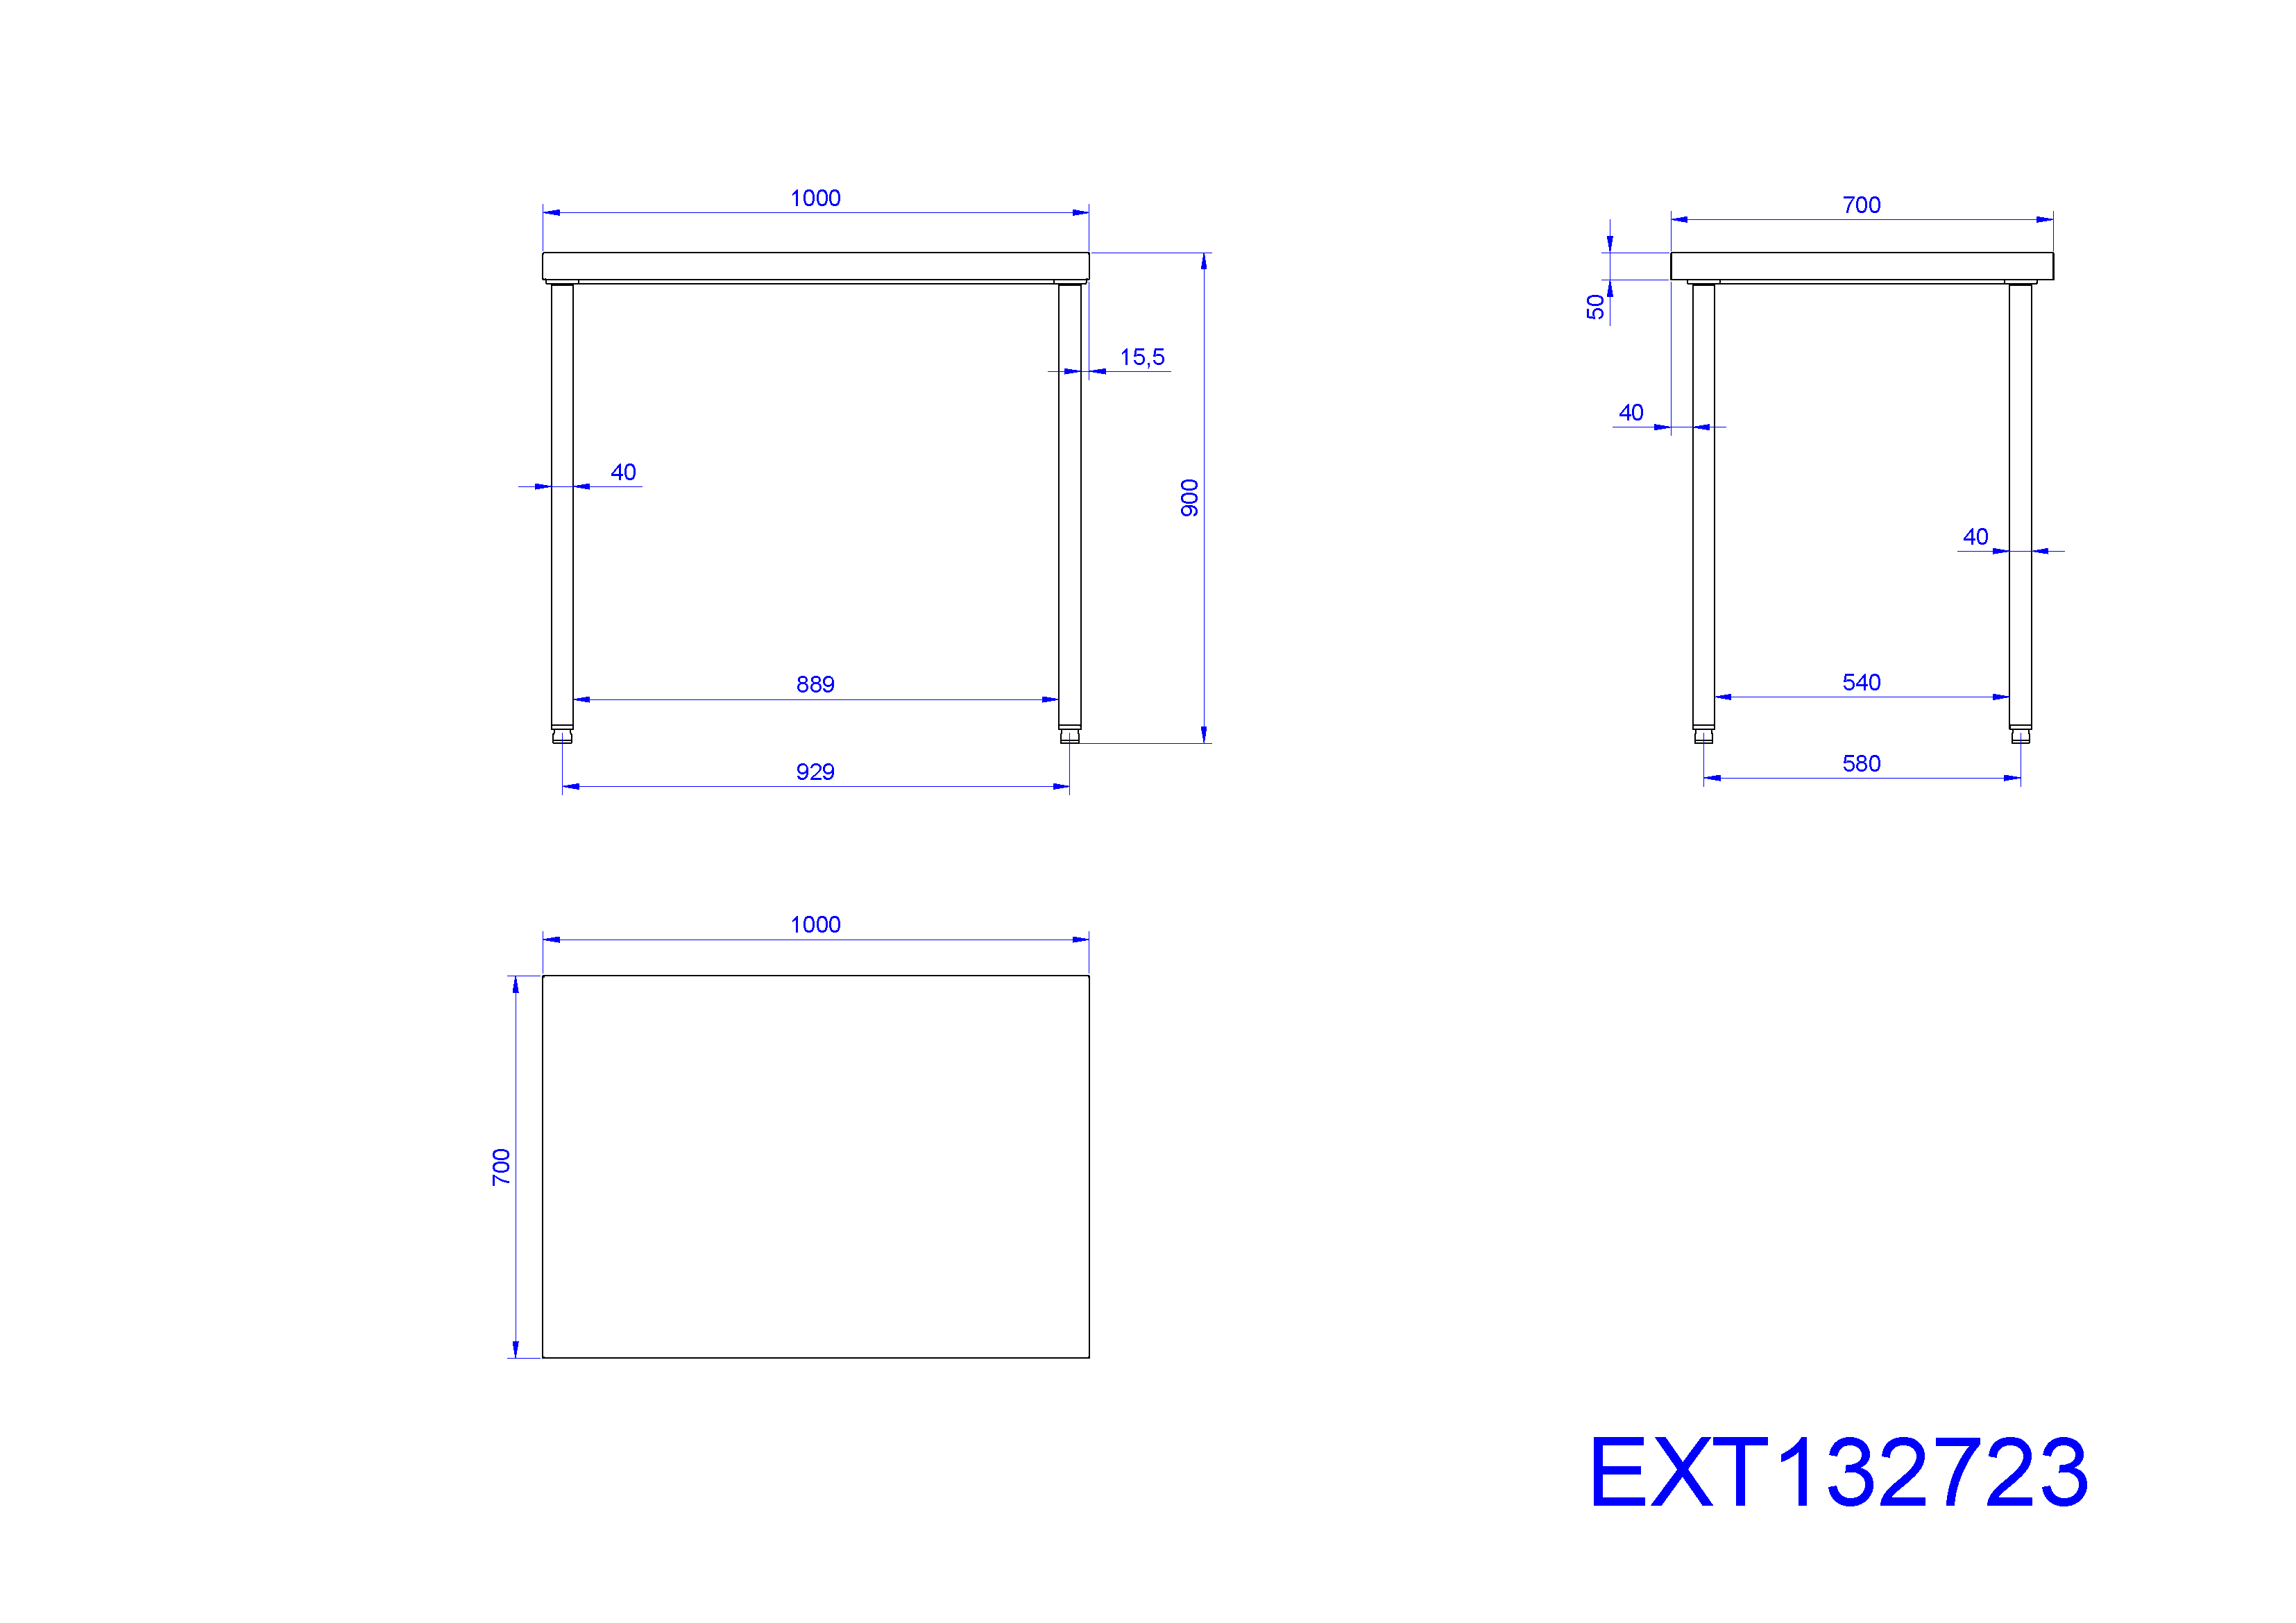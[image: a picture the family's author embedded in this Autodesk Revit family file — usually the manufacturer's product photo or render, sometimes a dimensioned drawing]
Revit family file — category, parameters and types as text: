
# Revit family: QF_ELECTROLUXPROFESSIONAL_132724_TG1200PN
name_source: partatom
category: Attrezzature speciali
units: mm (PartAtom-declared; Revit-internal decimal feet)

## family parameters
Basato su piano di lavoro = No
Condiviso = No
Punto di calcolo locali = No
Quota connettore circolare = Usa diametro
Sempre verticale = Sì
Taglio con vuoti quando caricato = No
Tipo di parte = Normale

## types (1)
- Standard
    Accessory = Sì
    Cold Water Size = 0 mm
    Compressed Air Pressure = 0.0 Pa
    Compressed Air Size = 0 mm
    Compressed Air Volume = 0.0 L/s
    Condensate Return Size = 0 mm
    Cycle = 0 Hz
    Depth Actual = 700 mm  [stored 2.29659 ft]
    Descrizione = WORK TABLE 1200 MM
    Direct Waste Size = 0 mm
    Gas Input Pressure = 0
    Gas KW = 0
    Gas Size = 0 mm
    HP = 0 HP
    Height Actual = 900 mm  [stored 2.95276 ft]
    Hot Water Size = 0 mm
    Item Number = 132724
    Length Actual = 1200 mm
    Modello = TG1200PN
    Phase = 0
    Produttore = Electrolux Professional
    Prospetto di default = 0 mm  [stored 0 ft]
    Refrigerant Compressor Remote = Sì
    Refrigeration Liquid Line Size = 0 mm  [stored 0 ft]
    Refrigeration Suction Line Size = 0 mm  [stored 0 ft]
    Steam Consumption per Hour = 0
    Steam Supply Maximum Pressure = 0.0 Pa
    Steam Supply Minimum Pressure = 0.0 Pa
    Steam Supply Size = 0 mm
    URL = https://www.electroluxprofessional.com
    URL Manufacturer = https://www.electroluxprofessional.com
    Volts = 0 V
    Watts = 0 W
    Weight = 40.00 kg

note: source unit labels omitted for Gas Input Pressure — the stored unit's dimension contradicts the parameter name (converter mislabeling)

note: [stored X ft] marks values corroborated as IEEE doubles in the binary element streams (Revit-internal decimal feet)

## geometry (parser evidence)
native form markers: Sweep x2
no freeform markers — native parametric forms only
